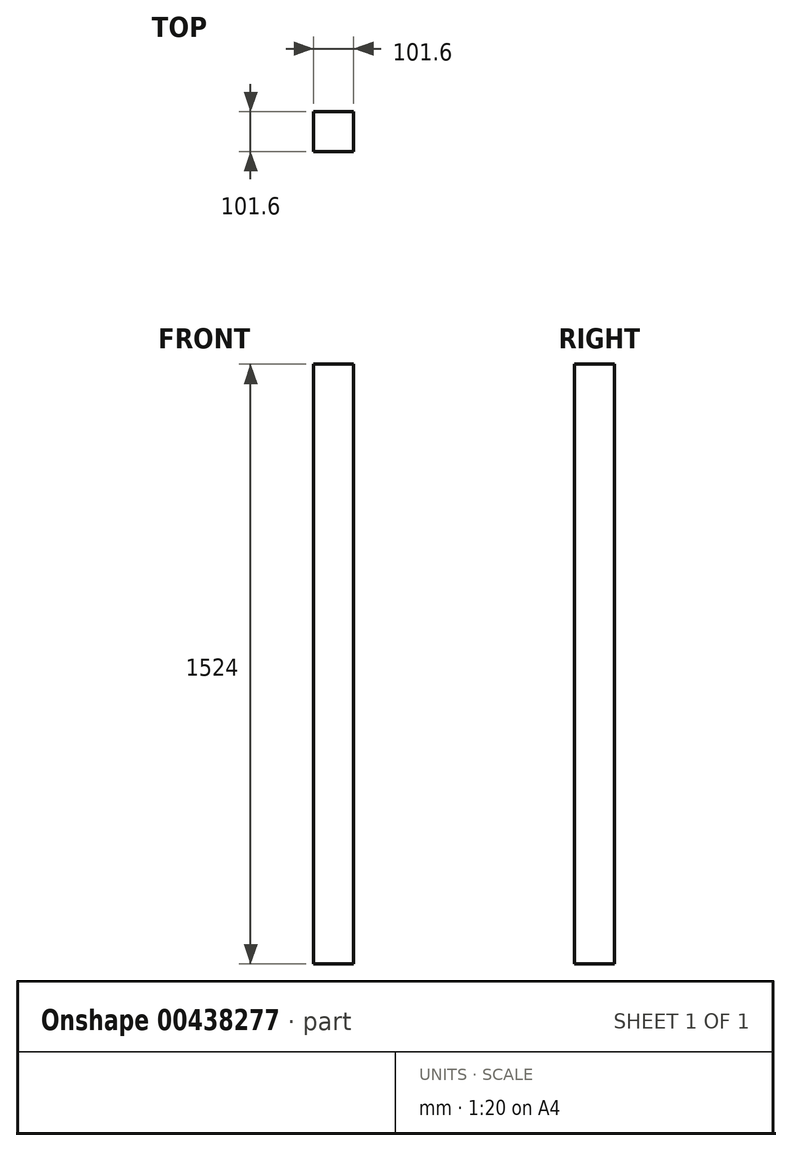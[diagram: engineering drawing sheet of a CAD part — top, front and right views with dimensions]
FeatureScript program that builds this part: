
annotation { "Feature Type Name" : "Feature", "Feature Type Description" : "" }
export const myFeature = defineFeature(function(context is Context, id is Id, definition is map)
    precondition{}
    {
        {
            var Q0;
            Q0=qCreatedBy(makeId("Front.planeOp"),FACE);
            var sketch = newSketch(context, id + "F0", { "sketchPlane" : qUnion([Q0])});
            skLineSegment(sketch, "E0.bottom", {"start": v(-50.8, 762) * mm, "end": v(50.8, 762) * mm});
            skLineSegment(sketch, "E0.top", {"start": v(-50.8, -762) * mm, "end": v(50.8, -762) * mm});
            skLineSegment(sketch, "E0.left", {"start": v(-50.8, 762) * mm, "end": v(-50.8, -762) * mm});
            skLineSegment(sketch, "E0.right", {"start": v(50.8, 762) * mm, "end": v(50.8, -762) * mm});
            skPoint(sketch, "E0.middle", {"position": v(0, 0) * mm});
            skSolve(sketch);
        }
        {
            var Q0;
            Q0 = qSketchRegion(id + "F0", true);
            extrude(context, id + "F1", {"entities" : qUnion([Q0]), "endBound" : BoundingType.SYMMETRIC, "depth" : 76.2 * mm});
        }
        {
            var Q0;
            Q0 = qSketchRegion(id + "F0", true);
            extrude(context, id + "F2", {"entities" : qUnion([Q0]), "operationType" : NewBodyOperationType.ADD, "endBound" : BoundingType.SYMMETRIC, "depth" : 101.6 * mm});
        }
    });
